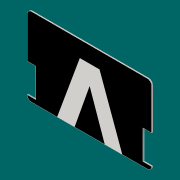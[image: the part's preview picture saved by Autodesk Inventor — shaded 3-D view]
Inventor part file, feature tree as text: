
AUTODESK INVENTOR PART (.ipt)
format: ipt  version: 2016 (Build 200138000, 138)  size: 215,552 bytes
history: native  units: mm
features: sketch x5, other x4, extrude x3, projected_geometry x3, fillet x1, mirror x1
ambient origin geometry x8: Origin, YZ Plane, XZ Plane, XY Plane, X Axis, Y Axis, Z Axis, Center Point
bodies: Solid1 (feature_tree)
feature tree (17):
  extrude  "Extrusion1"  Depth=53.98mm
  fillet  "Fillet1"  Radius=0.76mm
  extrude  "Extrusion2"  Depth=2.88mm
  extrude  "Extrusion3"  Depth=5.588mm
  mirror  "Mirror1"
  other  "Decal1"
  other  "Decal2"
  sketch  "Sketch1"  dims[d0=85.6mm d1=53.98mm d2=0.76mm]
  sketch  "Sketch2"  dims[d3=0.0mm d4=2.88mm]
  projected_geometry  "Projected Loop1"
  sketch  "Sketch3"  dims[d5=5.588mm d6=5.588mm]
  sketch  "Sketch4"  dims[d7=3.0mm]
  projected_geometry  "Projected Loop2"
  sketch  "Sketch5"  dims[d8=3.0mm d9=20.0mm d10=20.0mm d11=0.76mm d12=0.0mm d13=3.0mm d14=3.0mm d15=0.76mm d16=1.5mm d17=1.5mm d18=1.5mm d19=0.76mm d20=0.0mm]
  projected_geometry  "Projected Loop3"
  other  "Image4"
  other  "Image5"
